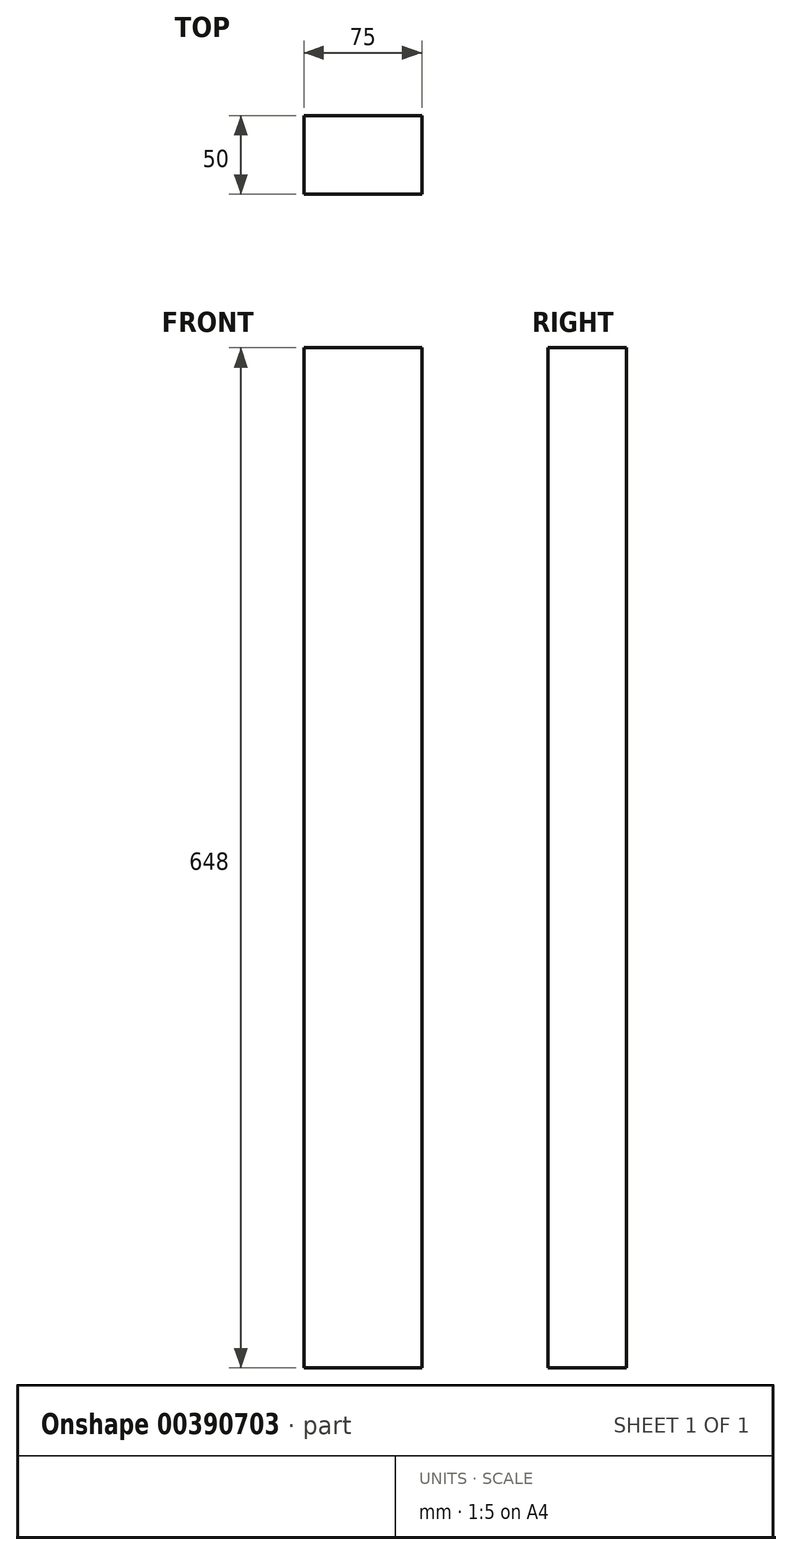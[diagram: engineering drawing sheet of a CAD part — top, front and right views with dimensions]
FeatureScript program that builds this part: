
annotation { "Feature Type Name" : "Feature", "Feature Type Description" : "" }
export const myFeature = defineFeature(function(context is Context, id is Id, definition is map)
    precondition{}
    {
        {
            var Q0;
            Q0=qCreatedBy(makeId("Top.planeOp"),FACE);
            var sketch = newSketch(context, id + "F0", { "sketchPlane" : qUnion([Q0])});
            skLineSegment(sketch, "E0.bottom", {"start": v(0, 0) * mm, "end": v(75, 0) * mm});
            skLineSegment(sketch, "E0.top", {"start": v(0, 50) * mm, "end": v(75, 50) * mm});
            skLineSegment(sketch, "E0.left", {"start": v(0, 0) * mm, "end": v(0, 50) * mm});
            skLineSegment(sketch, "E0.right", {"start": v(75, 0) * mm, "end": v(75, 50) * mm});
            skSolve(sketch);
        }
        {
            var Q0;
            Q0 = qSketchRegion(id + "F0", true);
            extrude(context, id + "F1", {"entities" : qUnion([Q0]), "depth" : 648 * mm});
        }
    });
